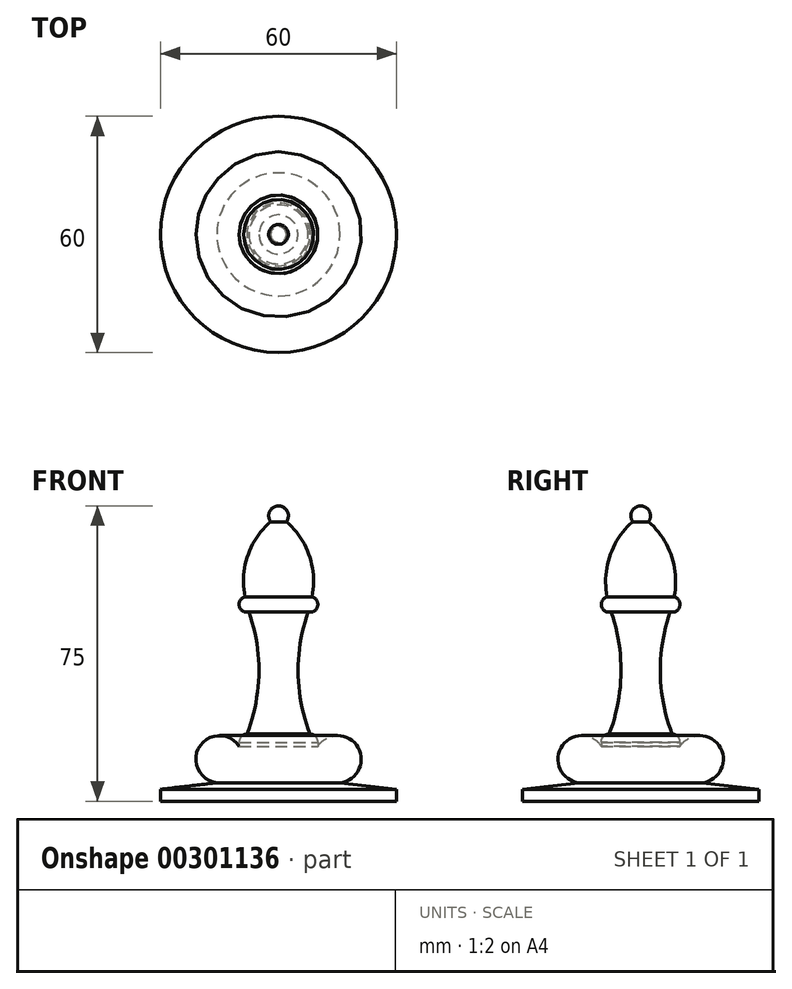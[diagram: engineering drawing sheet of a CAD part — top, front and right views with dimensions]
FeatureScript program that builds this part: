
annotation { "Feature Type Name" : "Feature", "Feature Type Description" : "" }
export const myFeature = defineFeature(function(context is Context, id is Id, definition is map)
    precondition{}
    {
        {
            var Q0;
            Q0=qCreatedBy(makeId("Front.planeOp"),FACE);
            var sketch = newSketch(context, id + "F0", { "sketchPlane" : qUnion([Q0])});
            skArc(sketch, "E0", {"start": v(2, -4) * mm, "mid": v(2.24, -1.38) * mm, "end": v(0, 0) * mm});
            skArc(sketch, "E1", {"start": v(8.5, -23.06) * mm, "mid": v(7.82, -12.65) * mm, "end": v(2, -4) * mm});
            skArc(sketch, "E2", {"start": v(8.5, -26.93) * mm, "mid": v(10, -25) * mm, "end": v(8.5, -23.06) * mm});
            skLineSegment(sketch, "E3", {"start": v(8.5, -26.93) * mm, "end": v(7.5, -26.93) * mm});
            skArc(sketch, "E4", {"start": v(7.5, -26.93) * mm, "mid": v(5, -42.49) * mm, "end": v(8, -57.95) * mm});
            skArc(sketch, "E5", {"start": v(10, -60.03) * mm, "mid": v(9.44, -58.57) * mm, "end": v(8, -57.95) * mm});
            skLineSegment(sketch, "E6", {"start": v(10, -60.03) * mm, "end": v(10, -61.03) * mm});
            skArc(sketch, "E7", {"start": v(13, -70) * mm, "mid": v(20.7, -62.44) * mm, "end": v(10, -61.03) * mm});
            skLineSegment(sketch, "E8", {"start": v(13, -70) * mm, "end": v(30, -72) * mm});
            skLineSegment(sketch, "E9", {"start": v(30, -72) * mm, "end": v(30, -75) * mm});
            skLineSegment(sketch, "E10", {"start": v(30, -75) * mm, "end": v(0, -75) * mm});
            skLineSegment(sketch, "E11", {"start": v(0, -75) * mm, "end": v(0, 0) * mm});
            skSolve(sketch);
        }
        {
            var Q0;
            Q0 = qSketchRegion(id + "F0", true);
            var Q1;
            Q1=sQuery(id+"F0.wireOp",EDGE,"E11");
            revolve(context, id + "F1", {"entities" : qUnion([Q0]), "axis" : qUnion([Q1]), "revolveType" : RevolveType.FULL});
        }
    });
